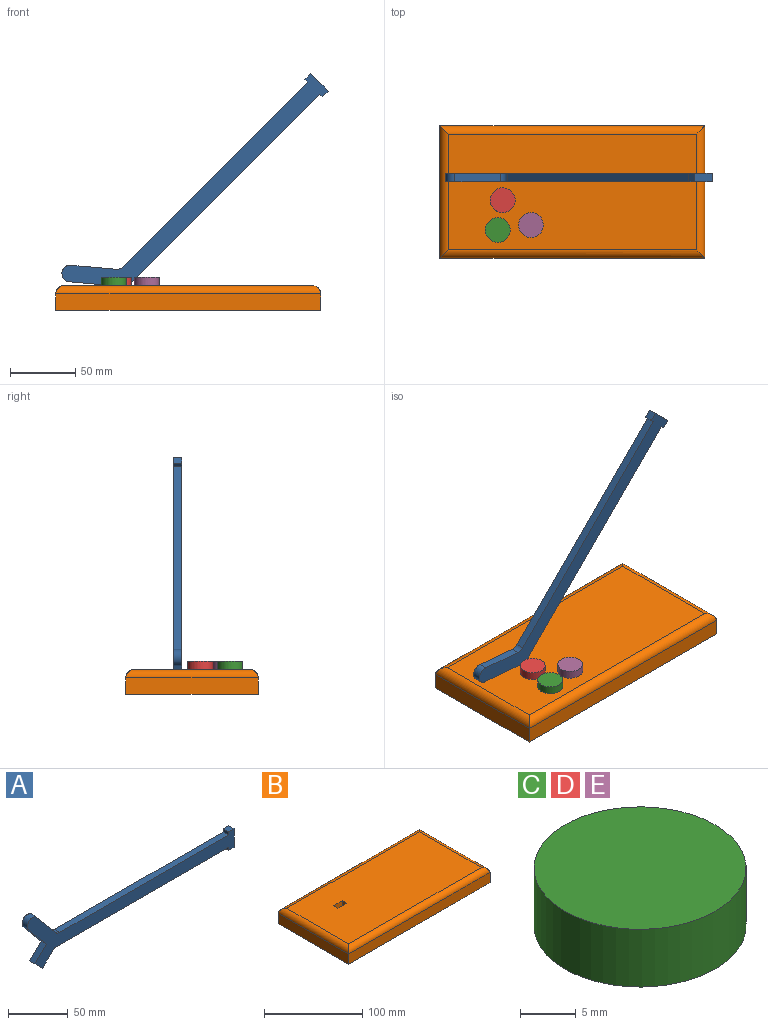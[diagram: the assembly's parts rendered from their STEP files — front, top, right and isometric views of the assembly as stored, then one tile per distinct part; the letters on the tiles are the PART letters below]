
ASSEMBLY  parts=5 mates=4
PART A: 17 faces, bbox 245.3x6.4x58.1 mm
  f0: cylinder r=6.35mm len=11.21mm, axis (0,1,0), area 126.7mm2, adj f1,f14,f15,f16
  f1: plane 25.15x21.11mm, normal (-0.77,0,-0.64), area 208.5mm2, adj f0,f2,f15,f16
  f2: plane 13.52x13.52mm, normal (-0.71,0,0.71), area 121.4mm2, adj f1,f3,f15,f16
  f3: plane 8.98x8.98mm, normal (-0.71,0,-0.71), area 80.6mm2, adj f2,f4,f15,f16
  f4: plane 14.37x14.37mm, normal (0.71,0,-0.71), area 129mm2, adj f3,f5,f15,f16
  f5: cylinder r=12.7mm len=6.35mm, axis (0,1,0), area 21.1mm2, adj f4,f6,f15,f16
  f6: plane 203.2x6.35mm, normal (0,0,-1), area 1290.3mm2, adj f5,f7,f15,f16
  f7: plane 6.35x3.18mm, normal (-1,0,0), area 20.2mm2, adj f6,f8,f15,f16
  f8: plane 6.35x6.35mm, normal (0,0,-1), area 40.3mm2, adj f7,f9,f15,f16
  f9: plane 19.05x6.35mm, normal (1,0,0), area 121mm2, adj f8,f10,f15,f16
  f10: plane 6.35x6.35mm, normal (0,0,1), area 40.3mm2, adj f9,f11,f15,f16
  f11: plane 6.35x3.18mm, normal (-1,0,0), area 20.2mm2, adj f10,f12,f15,f16
  f12: plane 200.24x6.35mm, normal (0,0,1), area 1271.5mm2, adj f11,f13,f15,f16
  f13: cylinder r=6.35mm len=6.35mm, axis (0,1,0), area 35.2mm2, adj f12,f14,f15,f16
  f14: plane 26.92x22.59mm, normal (0.77,0,0.64), area 223.1mm2, adj f0,f13,f15,f16
  f15: plane 245.25x58.09mm, normal (0,-1,0), area 3561.8mm2, adj f0,f1,f2,f3,f4,f5,f6,f7
  f16: plane 245.25x58.09mm, normal (0,1,0), area 3561.8mm2, adj f0,f1,f2,f3,f4,f5,f6,f7
PART B: 14 faces, bbox 203.2x101.6x19.1 mm
  f0: plane 203.2x12.7mm, normal (0,-1,0), area 2580.6mm2, adj f1,f3,f5,f6
  f1: plane 101.6x12.7mm, normal (1,0,0), area 1290.3mm2, adj f0,f2,f5,f7
  f2: plane 203.2x12.7mm, normal (0,1,0), area 2580.6mm2, adj f1,f3,f5,f9
  f3: plane 101.6x12.7mm, normal (-1,0,0), area 1290.3mm2, adj f0,f2,f5,f8
  f4: plane 190.5x88.9mm, normal (0,0,1), area 16854.8mm2, adj f6,f7,f8,f9,f10,f11,f12,f13
  f5: plane 203.2x101.6mm, normal (0,0,-1), area 20564.5mm2, adj f0,f1,f2,f3,f10,f11,f12,f13
  f6: cylinder r=6.35mm len=203.2mm, axis (-1,0,0), area 1980.8mm2, adj f0,f4,f7,f8
  f7: cylinder r=6.35mm len=101.6mm, axis (0,-1,0), area 967.4mm2, adj f1,f4,f6,f9
  f8: cylinder r=6.35mm len=101.6mm, axis (0,1,0), area 967.4mm2, adj f3,f4,f6,f9
  f9: cylinder r=6.35mm len=203.2mm, axis (1,0,0), area 1980.8mm2, adj f2,f4,f7,f8
  f10: plane 19.05x6.35mm, normal (-1,0,0), area 121mm2, adj f4,f5,f11,f12
  f11: plane 19.05x12.7mm, normal (0,1,0), area 241.9mm2, adj f4,f5,f10,f13
  f12: plane 19.05x12.7mm, normal (0,-1,0), area 241.9mm2, adj f4,f5,f10,f13
  f13: plane 19.05x6.35mm, normal (1,0,0), area 121mm2, adj f4,f5,f11,f12
PART C: 3 faces, bbox 19.1x19.1x6.4 mm
  f0: cylinder r=9.53mm len=19.05mm, axis (0,0,-1), area 380mm2, adj f1,f2
  f1: plane 19.05x19.05mm, normal (0,0,1), area 285mm2, adj f0
  f2: plane 19.05x19.05mm, normal (0,0,-1), area 285mm2, adj f0
PART D: same geometry as C
PART E: same geometry as C
PLACE A rot(axis=(0,-1,0),45deg) t=(-40.3,13.25,7.84)mm
PLACE B t=(2.79,0.55,-4.97)mm
PLACE C t=(-54.36,-30.07,4.56)mm
PLACE D t=(-50.55,-7.21,4.56)mm
PLACE E t=(-28.96,-26.26,4.56)mm
MATE fastened E.f0 <-> B.f4  axis (0,0,-1) through (-28.96,-26.26,4.56)mm
MATE fastened A.f3 <-> B.f5  axis (0,0,-1) through (-42.93,6.9,-14.49)mm
MATE fastened C.f0 <-> B.f4  axis (0,0,-1) through (-54.36,-30.07,4.56)mm
MATE fastened D.f0 <-> B.f4  axis (0,0,-1) through (-50.55,-7.21,4.56)mm
